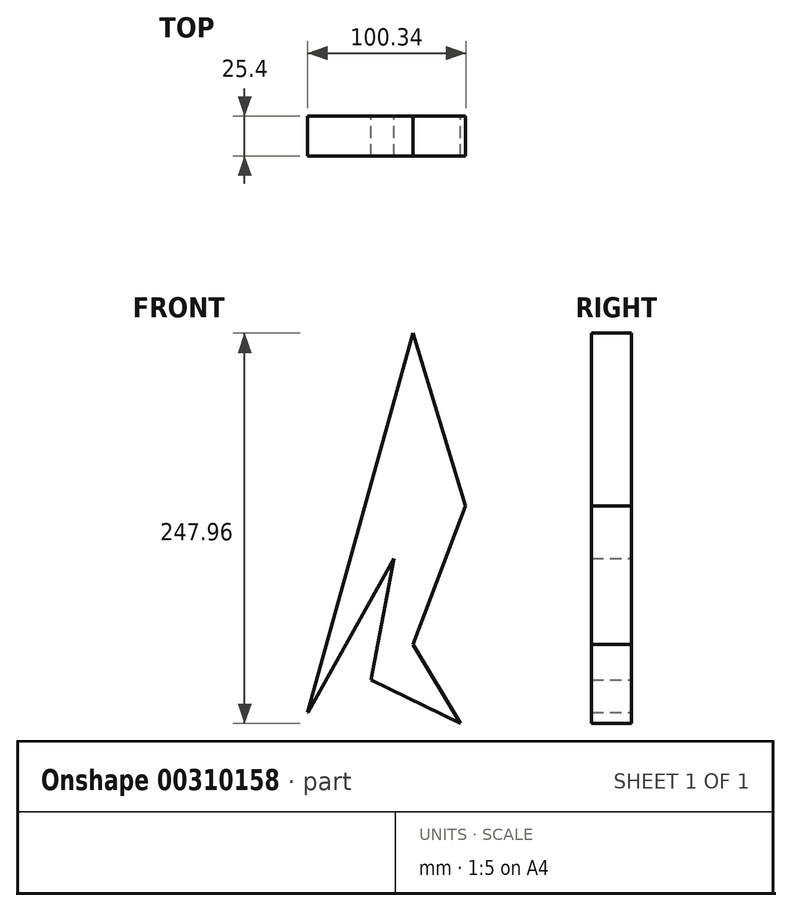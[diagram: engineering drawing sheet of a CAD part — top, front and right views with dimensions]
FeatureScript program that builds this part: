
annotation { "Feature Type Name" : "Feature", "Feature Type Description" : "" }
export const myFeature = defineFeature(function(context is Context, id is Id, definition is map)
    precondition{}
    {
        {
            var Q0;
            Q0=qCreatedBy(makeId("Front.planeOp"),FACE);
            var sketch = newSketch(context, id + "F0", { "sketchPlane" : qUnion([Q0])});
            skCircle(sketch, "E0", {"center": v(0, 0) * mm, "radius": 250.08 * mm});
            skSolve(sketch);
        }
        {
            var Q0;
            Q0=makeQuery(id+"F0.imprint","IMPRINT",FACE,{"disambiguationData":[TD([[makeQuery(id+"F0.imprint","IMPRINT",EDGE,{"derivedFrom":sQuery(id+"F0.wireOp",EDGE,"E0")}),1.0]])]});
            var sketch = newSketch(context, id + "F1", { "sketchPlane" : qUnion([Q0])});
            skLineSegment(sketch, "E1", {"start": v(0, 0) * mm, "end": v(-66.8, -241.23) * mm});
            skLineSegment(sketch, "E2", {"start": v(-66.8, -241.23) * mm, "end": v(-12.02, -143.13) * mm});
            skLineSegment(sketch, "E3", {"start": v(-12.02, -143.13) * mm, "end": v(-26.49, -220.3) * mm});
            skLineSegment(sketch, "E4", {"start": v(-26.49, -220.3) * mm, "end": v(30.32, -247.96) * mm});
            skLineSegment(sketch, "E5", {"start": v(30.32, -247.96) * mm, "end": v(0, -197.88) * mm});
            skLineSegment(sketch, "E6", {"start": v(0, -197.88) * mm, "end": v(33.6, -109.86) * mm});
            skLineSegment(sketch, "E7", {"start": v(33.6, -109.86) * mm, "end": v(0, 0) * mm});
            skSolve(sketch);
        }
        {
            var Q0;
            {var subQ0=sQuery(id+"F1.wireOp",EDGE,"E3");Q0=makeQuery(id+"F1.imprint","IMPRINT",FACE,{"disambiguationData":[TD([[makeQuery(id+"F1.imprint","IMPRINT",EDGE,{"derivedFrom":subQ0}),1.0]])]});}
            extrude(context, id + "F2", {"entities" : qUnion([Q0]), "depth" : 25.4 * mm});
        }
    });
